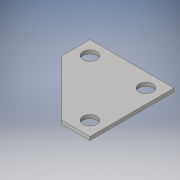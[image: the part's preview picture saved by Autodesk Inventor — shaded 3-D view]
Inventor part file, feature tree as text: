
AUTODESK INVENTOR PART (.ipt)
format: ipt  version: 2016 (Build 200138000, 138)  size: 107,520 bytes
history: native  units: in
note: dims shown in document units (in); Inventor stores cm internally (conversion verified against a paired STEP export)
features: extrude x1, sketch x1
ambient origin geometry x8: Origin, YZ Plane, XZ Plane, XY Plane, X Axis, Y Axis, Z Axis, Center Point
bodies: Solid1 (feature_tree)
feature tree (2):
  extrude  "Extrusion1"  Depth=3.0in
  sketch  "Sketch1"  dims[d0=3.0in d1=3.0in d2=2.0in d3=2.0in d4=0.5in d5=0.5in d6=0.5in d7=0.5in d8=2.0in d9=2.0in d10=0.5in d11=0.5in d12=0.5in d13=0.125in d14=0.0in]
